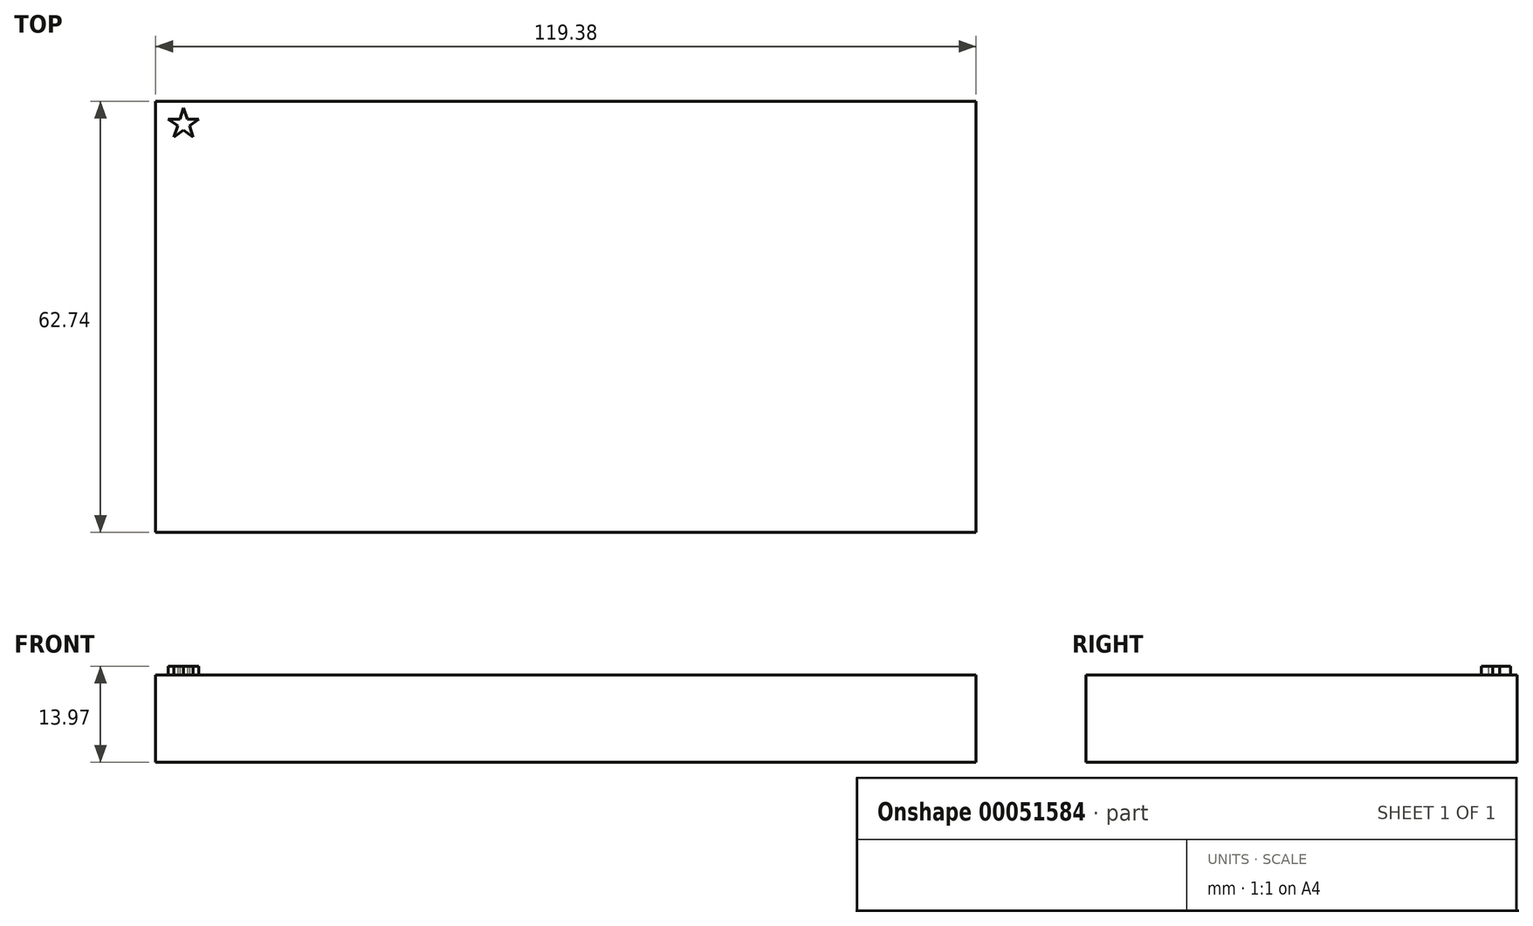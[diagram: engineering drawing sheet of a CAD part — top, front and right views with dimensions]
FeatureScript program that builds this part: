
annotation { "Feature Type Name" : "Feature", "Feature Type Description" : "" }
export const myFeature = defineFeature(function(context is Context, id is Id, definition is map)
    precondition{}
    {
        {
            var Q0;
            Q0=qCreatedBy(makeId("Top.planeOp"),FACE);
            var sketch = newSketch(context, id + "F0", { "sketchPlane" : qUnion([Q0])});
            skLineSegment(sketch, "E0.rect.bottom", {"start": v(59.7, 31.37) * mm, "end": v(-59.7, 31.37) * mm});
            skLineSegment(sketch, "E0.rect.top", {"start": v(59.7, -31.37) * mm, "end": v(-59.7, -31.37) * mm});
            skLineSegment(sketch, "E0.rect.left", {"start": v(59.7, 31.37) * mm, "end": v(59.7, -31.37) * mm});
            skLineSegment(sketch, "E0.rect.right", {"start": v(-59.7, 31.37) * mm, "end": v(-59.7, -31.37) * mm});
            skPoint(sketch, "E0.rect.middle", {"position": v(0, 0) * mm});
            skSolve(sketch);
        }
        {
            var Q0;
            Q0 = qSketchRegion(id + "F0", true);
            extrude(context, id + "F1", {"entities" : qUnion([Q0]), "depth" : 12.7 * mm});
        }
        {
            var Q0;
            Q0=makeQuery(id+"F1.opExtrude","CAP_FACE",FACE,{"disambiguationData":[OSD([sQuery(id+"F0.wireOp",EDGE,"E0.rect.bottom"),sQuery(id+"F0.wireOp",EDGE,"E0.rect.top"),sQuery(id+"F0.wireOp",EDGE,"E0.rect.left"),sQuery(id+"F0.wireOp",EDGE,"E0.rect.right")])],"isStart":false});
            var sketch = newSketch(context, id + "F2", { "sketchPlane" : qUnion([Q0])});
            skLineSegment(sketch, "E1.bottom", {"start": v(-59.7, 31.37) * mm, "end": v(-11.94, 31.37) * mm});
            skLineSegment(sketch, "E1.top", {"start": v(-59.7, -2.41) * mm, "end": v(-11.94, -2.41) * mm});
            skLineSegment(sketch, "E1.left", {"start": v(-59.7, 31.37) * mm, "end": v(-59.7, -2.41) * mm});
            skLineSegment(sketch, "E1.right", {"start": v(-11.94, 31.37) * mm, "end": v(-11.94, -2.41) * mm});
            skLineSegment(sketch, "E2.bottom", {"start": v(-11.94, 31.37) * mm, "end": v(59.7, 31.37) * mm});
            skLineSegment(sketch, "E2.top", {"start": v(-11.94, 26.54) * mm, "end": v(59.7, 26.54) * mm});
            skLineSegment(sketch, "E2.left", {"start": v(-11.94, 31.37) * mm, "end": v(-11.94, 26.54) * mm});
            skLineSegment(sketch, "E2.right", {"start": v(59.7, 31.37) * mm, "end": v(59.7, 26.54) * mm});
            skLineSegment(sketch, "E3.MirrorCS", {"start": v(-11.94, 21.72) * mm, "end": v(59.7, 21.72) * mm});
            skLineSegment(sketch, "E4.MirrorCS", {"start": v(-11.94, 16.9) * mm, "end": v(59.7, 16.9) * mm});
            skLineSegment(sketch, "E5.MirrorCS", {"start": v(-11.94, 12.06) * mm, "end": v(59.7, 12.06) * mm});
            skLineSegment(sketch, "E6.MirrorCS", {"start": v(-11.94, 7.24) * mm, "end": v(59.7, 7.24) * mm});
            skLineSegment(sketch, "E7.MirrorCS", {"start": v(-11.94, 2.41) * mm, "end": v(59.7, 2.41) * mm});
            skLineSegment(sketch, "E8.MirrorCS", {"start": v(-11.94, -2.41) * mm, "end": v(59.7, -2.41) * mm});
            skLineSegment(sketch, "E9.MirrorCS", {"start": v(-59.69, -7.24) * mm, "end": v(59.7, -7.24) * mm});
            skLineSegment(sketch, "E10.MirrorCS", {"start": v(-59.69, -12.07) * mm, "end": v(59.7, -12.07) * mm});
            skLineSegment(sketch, "E11.MirrorCS", {"start": v(-59.69, -16.9) * mm, "end": v(59.7, -16.9) * mm});
            skLineSegment(sketch, "E12.MirrorCS", {"start": v(-59.69, -21.72) * mm, "end": v(59.7, -21.72) * mm});
            skLineSegment(sketch, "E13.MirrorCS", {"start": v(-59.69, -26.54) * mm, "end": v(59.7, -26.54) * mm});
            skLineSegment(sketch, "E14", {"start": v(-55.63, 30.42) * mm, "end": v(-56.15, 28.8) * mm});
            skLineSegment(sketch, "E15", {"start": v(-57.01, 26.16) * mm, "end": v(-55.63, 27.17) * mm});
            skLineSegment(sketch, "E16", {"start": v(-53.39, 28.8) * mm, "end": v(-55.1, 28.8) * mm});
            skLineSegment(sketch, "E17", {"start": v(-57.87, 28.8) * mm, "end": v(-56.48, 27.79) * mm});
            skLineSegment(sketch, "E18", {"start": v(-54.24, 26.16) * mm, "end": v(-54.77, 27.79) * mm});
            skLineSegment(sketch, "E19.trimOffspring", {"start": v(-56.15, 28.8) * mm, "end": v(-57.87, 28.8) * mm});
            skLineSegment(sketch, "E20.trimOffspring", {"start": v(-56.48, 27.79) * mm, "end": v(-57.01, 26.16) * mm});
            skLineSegment(sketch, "E21.trimOffspring", {"start": v(-55.63, 27.17) * mm, "end": v(-54.24, 26.16) * mm});
            skLineSegment(sketch, "E22.trimOffspring", {"start": v(-54.77, 27.79) * mm, "end": v(-53.39, 28.8) * mm});
            skLineSegment(sketch, "E23.trimOffspring", {"start": v(-55.1, 28.8) * mm, "end": v(-55.63, 30.42) * mm});
            skSolve(sketch);
        }
        {
            var Q0;
            Q0=makeQuery(id+"F2.imprint","IMPRINT",FACE,{"disambiguationData":[TD([[makeQuery(id+"F2.imprint","IMPRINT",EDGE,{"derivedFrom":sQuery(id+"F2.wireOp",EDGE,"E14")}),1.0]])]});
            extrude(context, id + "F3", {"entities" : qUnion([Q0]), "operationType" : NewBodyOperationType.ADD, "depth" : 1.27 * mm});
        }
    });
